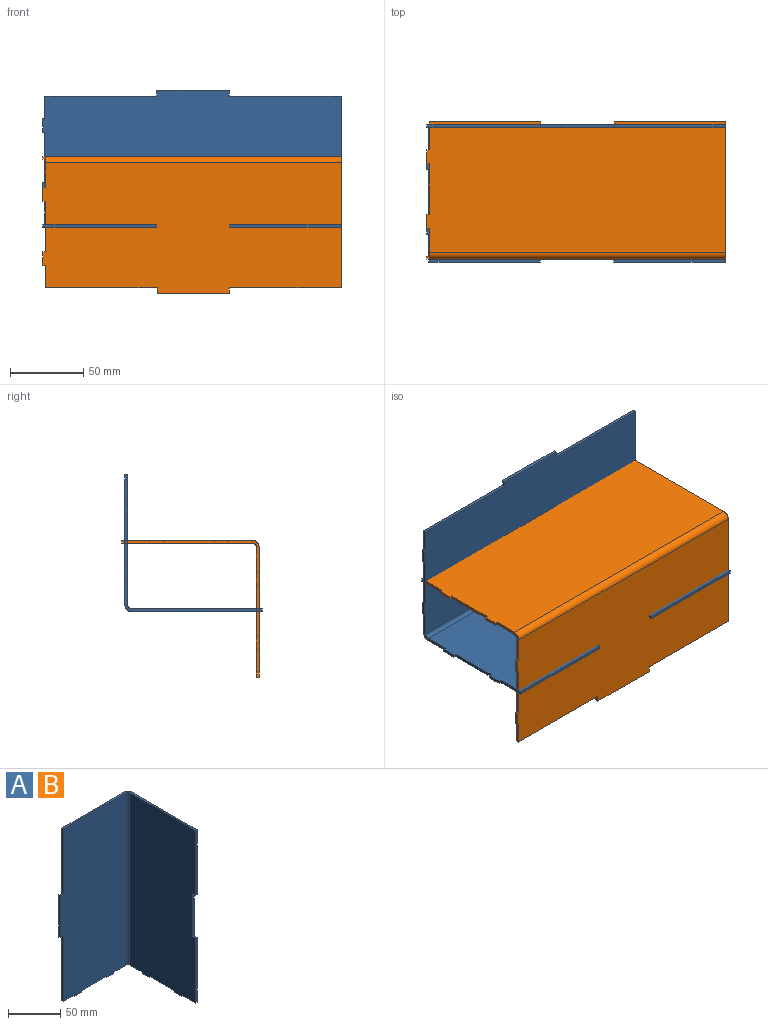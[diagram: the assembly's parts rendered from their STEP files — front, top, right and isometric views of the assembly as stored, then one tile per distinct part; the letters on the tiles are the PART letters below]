
ASSEMBLY  parts=2 mates=1
PART A: 38 faces, bbox 93.3x93.3x203.2 mm
  f0: plane 3.97x1.98mm, normal (0,0,-1), area 7.9mm2, adj f1,f14,f15,f16
  f1: plane 76.2x1.98mm, normal (-1,0,0), area 151.2mm2, adj f0,f2,f15,f16
  f2: plane 15.08x1.98mm, normal (0,0,-1), area 29.9mm2, adj f1,f3,f15,f16
  f3: plane 1.98x1.59mm, normal (-1,0,0), area 3.2mm2, adj f2,f4,f15,f16
  f4: plane 9.53x1.98mm, normal (0,0,-1), area 18.9mm2, adj f3,f5,f15,f16
  f5: plane 1.98x1.59mm, normal (1,0,0), area 3.2mm2, adj f4,f6,f15,f16
  f6: plane 34.21x1.98mm, normal (0,0,-1), area 67.9mm2, adj f5,f7,f15,f16
  f7: plane 1.98x1.59mm, normal (-1,0,0), area 3.2mm2, adj f6,f8,f15,f16
  f8: plane 9.53x1.98mm, normal (0,0,-1), area 18.9mm2, adj f7,f9,f15,f16
  f9: plane 1.98x1.59mm, normal (1,0,0), area 3.2mm2, adj f8,f10,f15,f16
  f10: plane 16.76x1.98mm, normal (0,0,-1), area 33.3mm2, adj f9,f15,f16,f35
  f11: plane 85.11x1.98mm, normal (0,0,1), area 168.9mm2, adj f12,f15,f16,f34
  f12: plane 76.2x1.98mm, normal (-1,0,0), area 151.2mm2, adj f11,f13,f15,f16
  f13: plane 3.97x1.98mm, normal (0,0,1), area 7.9mm2, adj f12,f14,f15,f16
  f14: plane 49.21x1.98mm, normal (-1,0,0), area 97.7mm2, adj f0,f13,f15,f16
  f15: plane 203.2x89.07mm, normal (0,-1,0), area 17384mm2, adj f0,f1,f2,f3,f4,f5,f6,f7
  f16: plane 203.2x89.07mm, normal (0,1,0), area 17384mm2, adj f0,f1,f2,f3,f4,f5,f6,f7
  f17: plane 89.07x1.98mm, normal (0,0,1), area 176.8mm2, adj f31,f32,f33,f34
  f18: plane 16.76x1.98mm, normal (0,0,-1), area 33.3mm2, adj f19,f32,f33,f35
  f19: plane 1.98x1.59mm, normal (0,1,0), area 3.2mm2, adj f18,f20,f32,f33
  f20: plane 9.53x1.98mm, normal (0,0,-1), area 18.9mm2, adj f19,f21,f32,f33
  f21: plane 1.98x1.59mm, normal (0,-1,0), area 3.2mm2, adj f20,f22,f32,f33
  f22: plane 34.21x1.98mm, normal (0,0,-1), area 67.9mm2, adj f21,f23,f32,f33
  f23: plane 1.98x1.59mm, normal (0,1,0), area 3.2mm2, adj f22,f24,f32,f33
  f24: plane 9.53x1.98mm, normal (0,0,-1), area 18.9mm2, adj f23,f25,f32,f33
  f25: plane 1.98x1.59mm, normal (0,-1,0), area 3.2mm2, adj f24,f26,f32,f33
  f26: plane 19.05x1.98mm, normal (0,0,-1), area 37.8mm2, adj f25,f27,f32,f33
  f27: plane 75.8x1.98mm, normal (0,-1,0), area 150.4mm2, adj f26,f28,f32,f33
  f28: plane 3.97x1.98mm, normal (0,0,1), area 7.9mm2, adj f27,f29,f32,f33
  f29: plane 50.01x1.98mm, normal (0,-1,0), area 99.2mm2, adj f28,f30,f32,f33
  f30: plane 3.97x1.98mm, normal (0,0,-1), area 7.9mm2, adj f29,f31,f32,f33
  f31: plane 75.8x1.98mm, normal (0,-1,0), area 150.4mm2, adj f17,f30,f32,f33
  f32: plane 203.2x89.07mm, normal (-1,0,0), area 17790.3mm2, adj f17,f18,f19,f20,f21,f22,f23,f24
  f33: plane 203.2x89.07mm, normal (1,0,0), area 17790.3mm2, adj f17,f18,f19,f20,f21,f22,f23,f24
  f34: plane 4.27x4.27mm, normal (0,0,1), area 10.2mm2, adj f11,f17,f36,f37
  f35: plane 4.27x4.27mm, normal (0,0,-1), area 10.2mm2, adj f10,f18,f36,f37
  f36: cylinder r=4.27mm len=201.61mm, axis (0,0,1), area 1352.4mm2, adj f16,f33,f34,f35
  f37: cylinder r=2.29mm len=201.61mm, axis (0,0,1), area 724mm2, adj f15,f32,f34,f35
PART B: same geometry as A
PLACE A rot(axis=(0,1,0),90deg) t=(-242.45,-147.58,-47.61)mm
PLACE B rot(axis=(-0.71,0,-0.71),180deg) t=(-242.28,-145.59,-92.64)mm
MATE fastened A.f29 <-> B.f15  axis (0,-1,0) through (-241.66,-190.28,-93.29)mm
